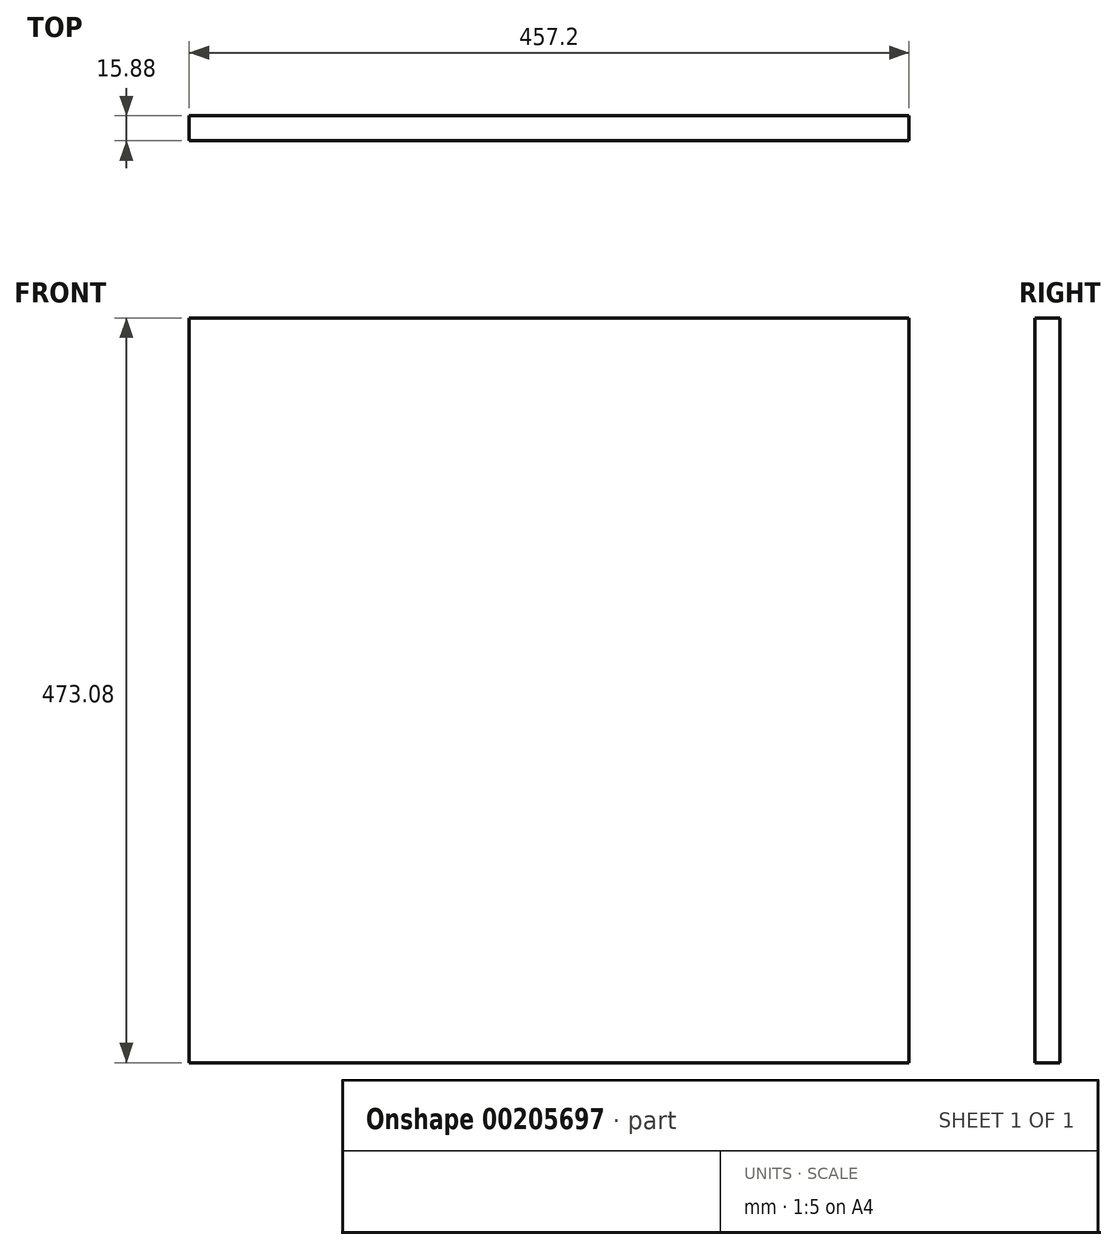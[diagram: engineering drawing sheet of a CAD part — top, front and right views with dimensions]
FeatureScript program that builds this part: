
annotation { "Feature Type Name" : "Feature", "Feature Type Description" : "" }
export const myFeature = defineFeature(function(context is Context, id is Id, definition is map)
    precondition{}
    {
        {
            var Q0;
            Q0=qCreatedBy(makeId("Front.planeOp"),FACE);
            var sketch = newSketch(context, id + "F0", { "sketchPlane" : qUnion([Q0])});
            skLineSegment(sketch, "E0.bottom", {"start": v(228.6, -236.54) * mm, "end": v(-228.6, -236.54) * mm});
            skLineSegment(sketch, "E0.top", {"start": v(228.6, 236.54) * mm, "end": v(-228.6, 236.54) * mm});
            skLineSegment(sketch, "E0.left", {"start": v(228.6, -236.54) * mm, "end": v(228.6, 236.54) * mm});
            skLineSegment(sketch, "E0.right", {"start": v(-228.6, -236.54) * mm, "end": v(-228.6, 236.54) * mm});
            skPoint(sketch, "E0.middle", {"position": v(0, 0) * mm});
            skSolve(sketch);
        }
        {
            var Q0;
            Q0=makeQuery(id+"F0.imprint","IMPRINT",FACE,{"disambiguationData":[TD([[makeQuery(id+"F0.imprint","IMPRINT",EDGE,{"derivedFrom":sQuery(id+"F0.wireOp",EDGE,"E0.bottom")}),-1.0]])]});
            extrude(context, id + "F1", {"entities" : qUnion([Q0]), "depth" : 15.88 * mm});
        }
    });
